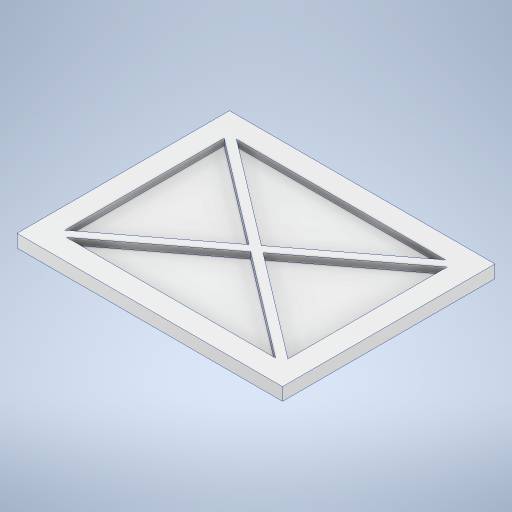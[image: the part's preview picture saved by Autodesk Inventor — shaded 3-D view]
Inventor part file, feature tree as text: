
AUTODESK INVENTOR PART (.ipt)
format: ipt  version: 2024 (Build 280153000, 153)  size: 270,848 bytes
history: native  units: mm
features: extrude x2, sketch x2, projected_geometry x1
ambient origin geometry x8: Origin, YZ Plane, XZ Plane, XY Plane, X Axis, Y Axis, Z Axis, Center Point
bodies: Solid1 (feature_tree)
feature tree (5):
  extrude  "Extrusion1"  Depth=250.0mm
  extrude  "Extrusion2"  Depth=20.0mm
  sketch  "Sketch1"  dims[d0=200.0mm d1=250.0mm]
  sketch  "Sketch2"  dims[d2=12.0mm d3=0.0mm d4=20.0mm d5=4.0mm d6=4.0mm d7=4.0mm d8=4.0mm d9=6.0mm d10=0.0mm]
  projected_geometry  "Projected Loop1"
